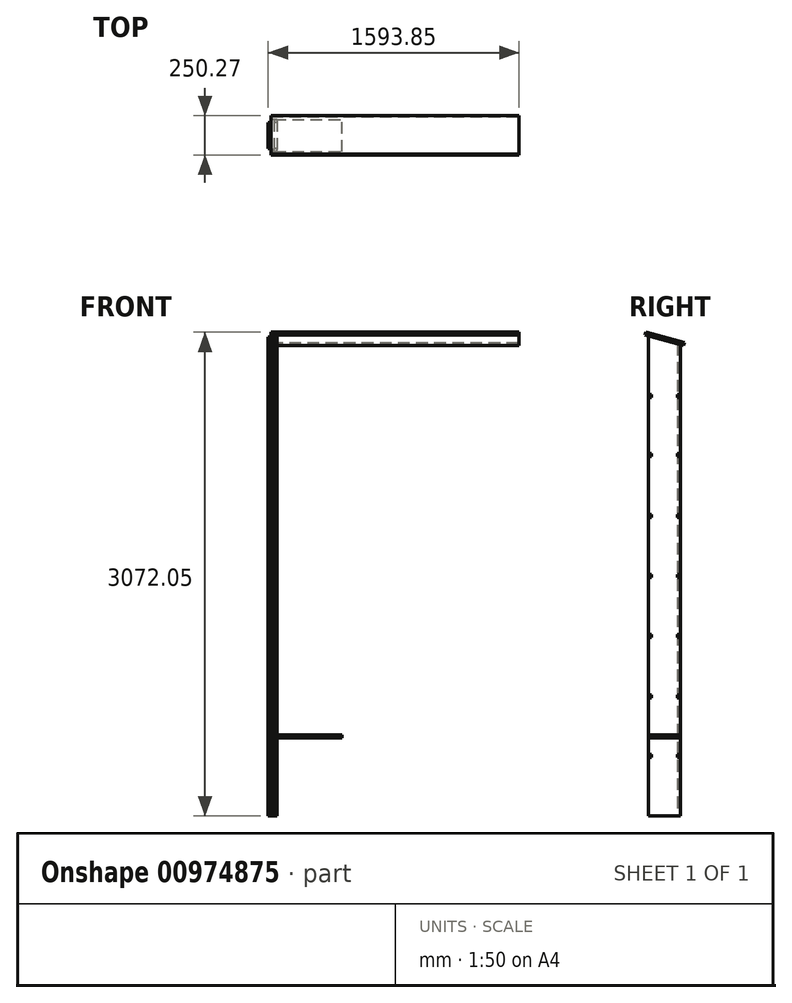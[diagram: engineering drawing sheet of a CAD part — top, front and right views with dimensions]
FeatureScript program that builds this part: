
annotation { "Feature Type Name" : "Feature", "Feature Type Description" : "" }
export const myFeature = defineFeature(function(context is Context, id is Id, definition is map)
    precondition{}
    {
        {
            assignVariable(context, id + "F0", {"name" : "Depth", "anyValue" : 203.2 * mm});
        }
        {
            var Q0;
            Q0=qCreatedBy(makeId("Front.planeOp"),FACE);
            var sketch = newSketch(context, id + "F1", { "sketchPlane" : qUnion([Q0])});
            skLineSegment(sketch, "E0.bottom", {"start": v(0, 0) * mm, "end": v(1524, 0) * mm});
            skLineSegment(sketch, "E0.top", {"start": v(0, 3048) * mm, "end": v(1524, 3048) * mm});
            skLineSegment(sketch, "E0.left", {"start": v(0, 0) * mm, "end": v(0, 3048) * mm});
            skLineSegment(sketch, "E0.right", {"start": v(1524, 0) * mm, "end": v(1524, 3048) * mm});
            skLineSegment(sketch, "E1", {"start": v(19.05, 3048) * mm, "end": v(19.05, 0) * mm});
            skLineSegment(sketch, "E2", {"start": v(38.1, 0) * mm, "end": v(38.1, 3048) * mm});
            skLineSegment(sketch, "E3", {"start": v(57.15, 3048) * mm, "end": v(57.15, 0) * mm});
            skLineSegment(sketch, "E4.bottom", {"start": v(57.15, 514.35) * mm, "end": v(488.95, 514.35) * mm});
            skLineSegment(sketch, "E4.top", {"start": v(57.15, 495.3) * mm, "end": v(488.95, 495.3) * mm});
            skLineSegment(sketch, "E4.left", {"start": v(57.15, 514.35) * mm, "end": v(57.15, 495.3) * mm});
            skLineSegment(sketch, "E4.right", {"start": v(488.95, 514.35) * mm, "end": v(488.95, 495.3) * mm});
            skLineSegment(sketch, "E5.bottom", {"start": v(488.95, 495.3) * mm, "end": v(57.15, 495.3) * mm});
            skLineSegment(sketch, "E5.top", {"start": v(488.95, 476.25) * mm, "end": v(57.15, 476.25) * mm});
            skLineSegment(sketch, "E5.left", {"start": v(488.95, 495.3) * mm, "end": v(488.95, 476.25) * mm});
            skLineSegment(sketch, "E5.right", {"start": v(57.15, 495.3) * mm, "end": v(57.15, 476.25) * mm});
            skLineSegment(sketch, "E6.bottom", {"start": v(57.15, 476.25) * mm, "end": v(488.95, 476.25) * mm});
            skLineSegment(sketch, "E6.top", {"start": v(57.15, 457.2) * mm, "end": v(488.95, 457.2) * mm});
            skLineSegment(sketch, "E6.left", {"start": v(57.15, 476.25) * mm, "end": v(57.15, 457.2) * mm});
            skLineSegment(sketch, "E6.right", {"start": v(488.95, 476.25) * mm, "end": v(488.95, 457.2) * mm});
            skLineSegment(sketch, "E7.bottom", {"start": v(488.95, 3048) * mm, "end": v(508, 3048) * mm});
            skLineSegment(sketch, "E7.top", {"start": v(488.95, 0) * mm, "end": v(508, 0) * mm});
            skLineSegment(sketch, "E7.left", {"start": v(488.95, 3048) * mm, "end": v(488.95, 0) * mm});
            skLineSegment(sketch, "E7.right", {"start": v(508, 3048) * mm, "end": v(508, 0) * mm});
            skSolve(sketch);
        }
        {
            var Q0;
            {var subQ0=sQuery(id+"F1.wireOp",EDGE,"E4.bottom");Q0=makeQuery(id+"F1.imprint","IMPRINT",FACE,{"disambiguationData":[TD([[makeQuery(id+"F1.imprint","IMPRINT",EDGE,{"derivedFrom":subQ0}),-1.0]])]});}
            extrude(context, id + "F2", {"entities" : qUnion([Q0]), "endBound" : BoundingType.SYMMETRIC, "depth" : getVariable(context, 'Depth'), "offsetDistance" : 25.4 * mm});
        }
        {
            var Q0;
            {var subQ0=sQuery(id+"F1.wireOp",EDGE,"E1");Q0=makeQuery(id+"F1.imprint","IMPRINT",FACE,{"disambiguationData":[TD([[makeQuery(id+"F1.imprint","IMPRINT",EDGE,{"derivedFrom":subQ0}),1.0]])]});}
            var Q1;
            {var subQ0=sQuery(id+"F1.wireOp",EDGE,"E5.bottom");Q1=makeQuery(id+"F1.imprint","IMPRINT",FACE,{"disambiguationData":[TD([[makeQuery(id+"F1.imprint","IMPRINT",EDGE,{"derivedFrom":subQ0}),1.0]])]});}
            extrude(context, id + "F3", {"entities" : qUnion([Q0, Q1]), "endBound" : BoundingType.SYMMETRIC, "depth" : getVariable(context, 'Depth') - 38.1 * mm, "offsetDistance" : 25.4 * mm});
        }
        {
            var Q0;
            {var subQ4=sQuery(id+"F1.wireOp",EDGE,"E2");Q0=makeQuery(id+"F1.imprint","IMPRINT",FACE,{"disambiguationData":[TD([[makeQuery(id+"F1.imprint","IMPRINT",EDGE,{"derivedFrom":subQ4}),-1.0]])]});}
            extrude(context, id + "F4", {"entities" : qUnion([Q0]), "endBound" : BoundingType.SYMMETRIC, "depth" : getVariable(context, 'Depth'), "offsetDistance" : 25.4 * mm});
        }
        {
            var Q0;
            Q0=makeQuery(id+"F4.opExtrude","SWEPT_FACE",FACE,{"disambiguationData":[OSD([sQuery(id+"F1.wireOp",EDGE,"E3"),sQuery(id+"F1.wireOp",EDGE,"E4.left"),sQuery(id+"F1.wireOp",EDGE,"E5.right"),sQuery(id+"F1.wireOp",EDGE,"E6.left")])]});
            var sketch = newSketch(context, id + "F5", { "sketchPlane" : qUnion([Q0])});
            skLineSegment(sketch, "E8.bottom", {"start": v(-101.6, 371.47) * mm, "end": v(-82.55, 371.47) * mm});
            skLineSegment(sketch, "E8.top", {"start": v(-101.6, 390.52) * mm, "end": v(-82.55, 390.52) * mm});
            skLineSegment(sketch, "E8.left", {"start": v(-101.6, 371.47) * mm, "end": v(-101.6, 390.52) * mm});
            skLineSegment(sketch, "E8.right", {"start": v(-82.55, 371.47) * mm, "end": v(-82.55, 390.52) * mm});
            skLineSegment(sketch, "E9.bottom", {"start": v(101.6, 390.52) * mm, "end": v(82.55, 390.52) * mm});
            skLineSegment(sketch, "E9.top", {"start": v(101.6, 371.47) * mm, "end": v(82.55, 371.47) * mm});
            skLineSegment(sketch, "E9.left", {"start": v(101.6, 390.52) * mm, "end": v(101.6, 371.47) * mm});
            skLineSegment(sketch, "E9.right", {"start": v(82.55, 390.52) * mm, "end": v(82.55, 371.47) * mm});
            skLineSegment(sketch, "E10.0.1.0", {"start": v(101.6, 1133.47) * mm, "end": v(82.55, 1133.47) * mm});
            skLineSegment(sketch, "E10.0.1.1", {"start": v(-101.6, 1133.47) * mm, "end": v(-82.55, 1133.47) * mm});
            skLineSegment(sketch, "E10.0.1.2", {"start": v(101.6, 1152.52) * mm, "end": v(82.55, 1152.52) * mm});
            skLineSegment(sketch, "E10.0.1.3", {"start": v(82.55, 1152.52) * mm, "end": v(82.55, 1133.47) * mm});
            skLineSegment(sketch, "E10.0.1.4", {"start": v(-101.6, 1133.47) * mm, "end": v(-101.6, 1152.52) * mm});
            skLineSegment(sketch, "E10.0.1.5", {"start": v(-101.6, 1152.52) * mm, "end": v(-82.55, 1152.52) * mm});
            skLineSegment(sketch, "E10.0.1.6", {"start": v(101.6, 1152.52) * mm, "end": v(101.6, 1133.47) * mm});
            skLineSegment(sketch, "E10.0.1.7", {"start": v(-82.55, 1133.47) * mm, "end": v(-82.55, 1152.52) * mm});
            skLineSegment(sketch, "E10.0.2.0", {"start": v(101.6, 1895.47) * mm, "end": v(82.55, 1895.47) * mm});
            skLineSegment(sketch, "E10.0.2.1", {"start": v(-101.6, 1895.47) * mm, "end": v(-82.55, 1895.47) * mm});
            skLineSegment(sketch, "E10.0.2.2", {"start": v(101.6, 1914.52) * mm, "end": v(82.55, 1914.52) * mm});
            skLineSegment(sketch, "E10.0.2.3", {"start": v(82.55, 1914.52) * mm, "end": v(82.55, 1895.47) * mm});
            skLineSegment(sketch, "E10.0.2.4", {"start": v(-101.6, 1895.47) * mm, "end": v(-101.6, 1914.52) * mm});
            skLineSegment(sketch, "E10.0.2.5", {"start": v(-101.6, 1914.52) * mm, "end": v(-82.55, 1914.52) * mm});
            skLineSegment(sketch, "E10.0.2.6", {"start": v(101.6, 1914.52) * mm, "end": v(101.6, 1895.47) * mm});
            skLineSegment(sketch, "E10.0.2.7", {"start": v(-82.55, 1895.47) * mm, "end": v(-82.55, 1914.52) * mm});
            skLineSegment(sketch, "E10.0.3.0", {"start": v(101.6, 2657.47) * mm, "end": v(82.55, 2657.47) * mm});
            skLineSegment(sketch, "E10.0.3.1", {"start": v(-101.6, 2657.47) * mm, "end": v(-82.55, 2657.47) * mm});
            skLineSegment(sketch, "E10.0.3.2", {"start": v(101.6, 2676.52) * mm, "end": v(82.55, 2676.52) * mm});
            skLineSegment(sketch, "E10.0.3.3", {"start": v(82.55, 2676.52) * mm, "end": v(82.55, 2657.47) * mm});
            skLineSegment(sketch, "E10.0.3.4", {"start": v(-101.6, 2657.47) * mm, "end": v(-101.6, 2676.52) * mm});
            skLineSegment(sketch, "E10.0.3.5", {"start": v(-101.6, 2676.52) * mm, "end": v(-82.55, 2676.52) * mm});
            skLineSegment(sketch, "E10.0.3.6", {"start": v(101.6, 2676.52) * mm, "end": v(101.6, 2657.47) * mm});
            skLineSegment(sketch, "E10.0.3.7", {"start": v(-82.55, 2657.47) * mm, "end": v(-82.55, 2676.52) * mm});
            skLineSegment(sketch, "E10.direction1", {"start": v(-101.6, 371.47) * mm, "end": v(-76.2, 371.47) * mm, "construction": true});
            skLineSegment(sketch, "E10.direction2", {"start": v(-101.6, 371.47) * mm, "end": v(-101.6, 1133.47) * mm, "construction": true});
            skSolve(sketch);
        }
        {
            var Q0;
            {var subQ10=sQuery(id+"F5.wireOp",EDGE,"E8.bottom");Q0=makeQuery(id+"F5.imprint","IMPRINT",FACE,{"disambiguationData":[TD([[makeQuery(id+"F5.imprint","IMPRINT",EDGE,{"derivedFrom":subQ10}),-1.0]])]});}
            extrude(context, id + "F6", {"entities" : qUnion([Q0]), "depth" : 19.05 * mm, "offsetDistance" : 25.4 * mm});
        }
        {
            var Q0;
            Q0=makeQuery(id+"F4.opExtrude","SWEPT_FACE",FACE,{"disambiguationData":[OSD([sQuery(id+"F1.wireOp",EDGE,"E3"),sQuery(id+"F1.wireOp",EDGE,"E4.left"),sQuery(id+"F1.wireOp",EDGE,"E5.right"),sQuery(id+"F1.wireOp",EDGE,"E6.left")])]});
            var sketch = newSketch(context, id + "F7", { "sketchPlane" : qUnion([Q0])});
            skLineSegment(sketch, "E11.bottom", {"start": v(-101.6, 0) * mm, "end": v(-82.55, 0) * mm});
            skLineSegment(sketch, "E11.top", {"start": v(-101.6, -19.05) * mm, "end": v(-82.55, -19.05) * mm});
            skLineSegment(sketch, "E11.left", {"start": v(-101.6, 0) * mm, "end": v(-101.6, -19.05) * mm});
            skLineSegment(sketch, "E11.right", {"start": v(-82.55, 0) * mm, "end": v(-82.55, -19.05) * mm});
            skLineSegment(sketch, "E12.bottom", {"start": v(101.6, 0) * mm, "end": v(82.55, 0) * mm});
            skLineSegment(sketch, "E12.top", {"start": v(101.6, -19.05) * mm, "end": v(82.55, -19.05) * mm});
            skLineSegment(sketch, "E12.left", {"start": v(101.6, 0) * mm, "end": v(101.6, -19.05) * mm});
            skLineSegment(sketch, "E12.right", {"start": v(82.55, 0) * mm, "end": v(82.55, -19.05) * mm});
            skLineSegment(sketch, "E13.0.1.0", {"start": v(-101.6, 766.76) * mm, "end": v(-82.55, 766.76) * mm});
            skLineSegment(sketch, "E13.0.1.1", {"start": v(101.6, 766.76) * mm, "end": v(82.55, 766.76) * mm});
            skLineSegment(sketch, "E13.0.1.2", {"start": v(-101.6, 747.71) * mm, "end": v(-82.55, 747.71) * mm});
            skLineSegment(sketch, "E13.0.1.3", {"start": v(101.6, 766.76) * mm, "end": v(101.6, 747.71) * mm});
            skLineSegment(sketch, "E13.0.1.4", {"start": v(101.6, 747.71) * mm, "end": v(82.55, 747.71) * mm});
            skLineSegment(sketch, "E13.0.1.5", {"start": v(-101.6, 766.76) * mm, "end": v(-101.6, 747.71) * mm});
            skLineSegment(sketch, "E13.0.1.6", {"start": v(-82.55, 766.76) * mm, "end": v(-82.55, 747.71) * mm});
            skLineSegment(sketch, "E13.0.1.7", {"start": v(82.55, 766.76) * mm, "end": v(82.55, 747.71) * mm});
            skLineSegment(sketch, "E13.0.2.0", {"start": v(-101.6, 1533.52) * mm, "end": v(-82.55, 1533.52) * mm});
            skLineSegment(sketch, "E13.0.2.1", {"start": v(101.6, 1533.52) * mm, "end": v(82.55, 1533.52) * mm});
            skLineSegment(sketch, "E13.0.2.2", {"start": v(-101.6, 1514.47) * mm, "end": v(-82.55, 1514.47) * mm});
            skLineSegment(sketch, "E13.0.2.3", {"start": v(101.6, 1533.52) * mm, "end": v(101.6, 1514.47) * mm});
            skLineSegment(sketch, "E13.0.2.4", {"start": v(101.6, 1514.47) * mm, "end": v(82.55, 1514.47) * mm});
            skLineSegment(sketch, "E13.0.2.5", {"start": v(-101.6, 1533.52) * mm, "end": v(-101.6, 1514.47) * mm});
            skLineSegment(sketch, "E13.0.2.6", {"start": v(-82.55, 1533.52) * mm, "end": v(-82.55, 1514.47) * mm});
            skLineSegment(sketch, "E13.0.2.7", {"start": v(82.55, 1533.52) * mm, "end": v(82.55, 1514.47) * mm});
            skLineSegment(sketch, "E13.0.3.0", {"start": v(-101.6, 2300.29) * mm, "end": v(-82.55, 2300.29) * mm});
            skLineSegment(sketch, "E13.0.3.1", {"start": v(101.6, 2300.29) * mm, "end": v(82.55, 2300.29) * mm});
            skLineSegment(sketch, "E13.0.3.2", {"start": v(-101.6, 2281.24) * mm, "end": v(-82.55, 2281.24) * mm});
            skLineSegment(sketch, "E13.0.3.3", {"start": v(101.6, 2300.29) * mm, "end": v(101.6, 2281.24) * mm});
            skLineSegment(sketch, "E13.0.3.4", {"start": v(101.6, 2281.24) * mm, "end": v(82.55, 2281.24) * mm});
            skLineSegment(sketch, "E13.0.3.5", {"start": v(-101.6, 2300.29) * mm, "end": v(-101.6, 2281.24) * mm});
            skLineSegment(sketch, "E13.0.3.6", {"start": v(-82.55, 2300.29) * mm, "end": v(-82.55, 2281.24) * mm});
            skLineSegment(sketch, "E13.0.3.7", {"start": v(82.55, 2300.29) * mm, "end": v(82.55, 2281.24) * mm});
            skLineSegment(sketch, "E13.0.4.0", {"start": v(-101.6, 3067.05) * mm, "end": v(-82.55, 3067.05) * mm});
            skLineSegment(sketch, "E13.0.4.1", {"start": v(101.6, 3067.05) * mm, "end": v(82.55, 3067.05) * mm});
            skLineSegment(sketch, "E13.0.4.2", {"start": v(-101.6, 3048) * mm, "end": v(-82.55, 3048) * mm});
            skLineSegment(sketch, "E13.0.4.3", {"start": v(101.6, 3067.05) * mm, "end": v(101.6, 3048) * mm});
            skLineSegment(sketch, "E13.0.4.4", {"start": v(101.6, 3048) * mm, "end": v(82.55, 3048) * mm});
            skLineSegment(sketch, "E13.0.4.5", {"start": v(-101.6, 3067.05) * mm, "end": v(-101.6, 3048) * mm});
            skLineSegment(sketch, "E13.0.4.6", {"start": v(-82.55, 3067.05) * mm, "end": v(-82.55, 3048) * mm});
            skLineSegment(sketch, "E13.0.4.7", {"start": v(82.55, 3067.05) * mm, "end": v(82.55, 3048) * mm});
            skLineSegment(sketch, "E13.direction1", {"start": v(-101.6, -19.05) * mm, "end": v(-76.2, -19.05) * mm, "construction": true});
            skLineSegment(sketch, "E13.direction2", {"start": v(-101.6, -19.05) * mm, "end": v(-101.6, 747.71) * mm, "construction": true});
            skSolve(sketch);
        }
        {
            var Q0;
            {var subQ11=sQuery(id+"F7.wireOp",EDGE,"E11.bottom");Q0=makeQuery(id+"F7.imprint","IMPRINT",FACE,{"disambiguationData":[TD([[makeQuery(id+"F7.imprint","IMPRINT",EDGE,{"derivedFrom":subQ11}),1.0]])]});}
            extrude(context, id + "F8", {"entities" : qUnion([Q0]), "depth" : 19.05 * mm, "offsetDistance" : 25.4 * mm});
        }
        {
            var Q0;
            Q0=makeQuery(id+"F4.opExtrude","SWEPT_FACE",FACE,{"disambiguationData":[OSD([sQuery(id+"F1.wireOp",EDGE,"E2")])]});
            var sketch = newSketch(context, id + "F9", { "sketchPlane" : qUnion([Q0])});
            skLineSegment(sketch, "E14", {"start": v(101.6, 3048) * mm, "end": v(-101.6, 2993.55) * mm});
            skSolve(sketch);
        }
        {
            var Q0;
            {var subQ0=sQuery(id+"F9.wireOp",EDGE,"E14");Q0=makeQuery(id+"F9.imprint","IMPRINT",FACE,{"disambiguationData":[TD([[makeQuery(id+"F9.imprint","IMPRINT",EDGE,{"derivedFrom":subQ0}),-1.0]])]});}
            extrude(context, id + "F10", {"entities" : qUnion([Q0]), "operationType" : NewBodyOperationType.REMOVE, "endBound" : BoundingType.THROUGH_ALL, "oppositeDirection" : true, "depth" : 25.4 * mm, "offsetDistance" : 25.4 * mm, "hasSecondDirection" : true, "secondDirectionBound" : SecondDirectionBoundingType.THROUGH_ALL, "secondDirectionOppositeDirection" : false, "secondDirectionDepth" : 25.4 * mm});
        }
        {
            var Q0;
            {var subQ4=sQuery(id+"F1.wireOp",EDGE,"E2");Q0=makeQuery(id+"F10.boolean.opBoolean","COPY",FACE,{"disambiguationData":[TD([makeQuery(id+"F4.opExtrude","SWEPT_FACE",FACE,{"disambiguationData":[OSD([subQ4])]})])],"derivedFrom":makeQuery(id+"F10.opExtrude","SWEPT_FACE",FACE,{"disambiguationData":[OSD([sQuery(id+"F9.wireOp",EDGE,"E14")])]})});}
            var sketch = newSketch(context, id + "F11", { "sketchPlane" : qUnion([Q0])});
            skLineSegment(sketch, "E15.bottom", {"start": v(38.1, -908.83) * mm, "end": v(1612.9, -908.83) * mm});
            skLineSegment(sketch, "E15.top", {"start": v(38.1, -654.83) * mm, "end": v(1612.9, -654.83) * mm});
            skLineSegment(sketch, "E15.left", {"start": v(38.1, -908.83) * mm, "end": v(38.1, -654.83) * mm});
            skLineSegment(sketch, "E15.right", {"start": v(1612.9, -908.83) * mm, "end": v(1612.9, -654.83) * mm});
            skPoint(sketch, "E16", {"position": v(1562.1, -908.83) * mm});
            skPoint(sketch, "E17", {"position": v(38.1, -781.83) * mm});
            skSolve(sketch);
        }
        {
            var Q0;
            {var subQ12=sQuery(id+"F11.wireOp",EDGE,"E15.bottom");Q0=makeQuery(id+"F11.imprint","IMPRINT",FACE,{"disambiguationData":[TD([[makeQuery(id+"F11.imprint","IMPRINT",EDGE,{"derivedFrom":subQ12}),1.0]])]});}
            var Q1;
            {var subQ1=sQuery(id+"F9.wireOp",EDGE,"E14");var subQ2=sQuery(id+"F1.wireOp",EDGE,"E2");var subQ3=sQuery(id+"F1.wireOp",EDGE,"E0.top");var subQ4=makeQuery(id+"F10.boolean.opBoolean","MERGE",EDGE,{"derivedFrom":[makeQuery(id+"F4.opExtrude","CAP_EDGE",EDGE,{"disambiguationData":[OSD([subQ3])],"isStart":false})],"fromTools":[makeQuery(id+"F10.opExtrude","SWEPT_EDGE",EDGE,{"disambiguationData":[OSD([subQ3,subQ2,subQ1])]})]});Q1=makeQuery(id+"F11.imprint","IMPRINT",FACE,{"disambiguationData":[TD([[makeQuery(id+"F11.imprint","IMPRINT",EDGE,{"derivedFrom":subQ4}),1.0]])]});}
            extrude(context, id + "F12", {"entities" : qUnion([Q0, Q1]), "depth" : 19.05 * mm, "offsetDistance" : 25.4 * mm});
        }
    });
